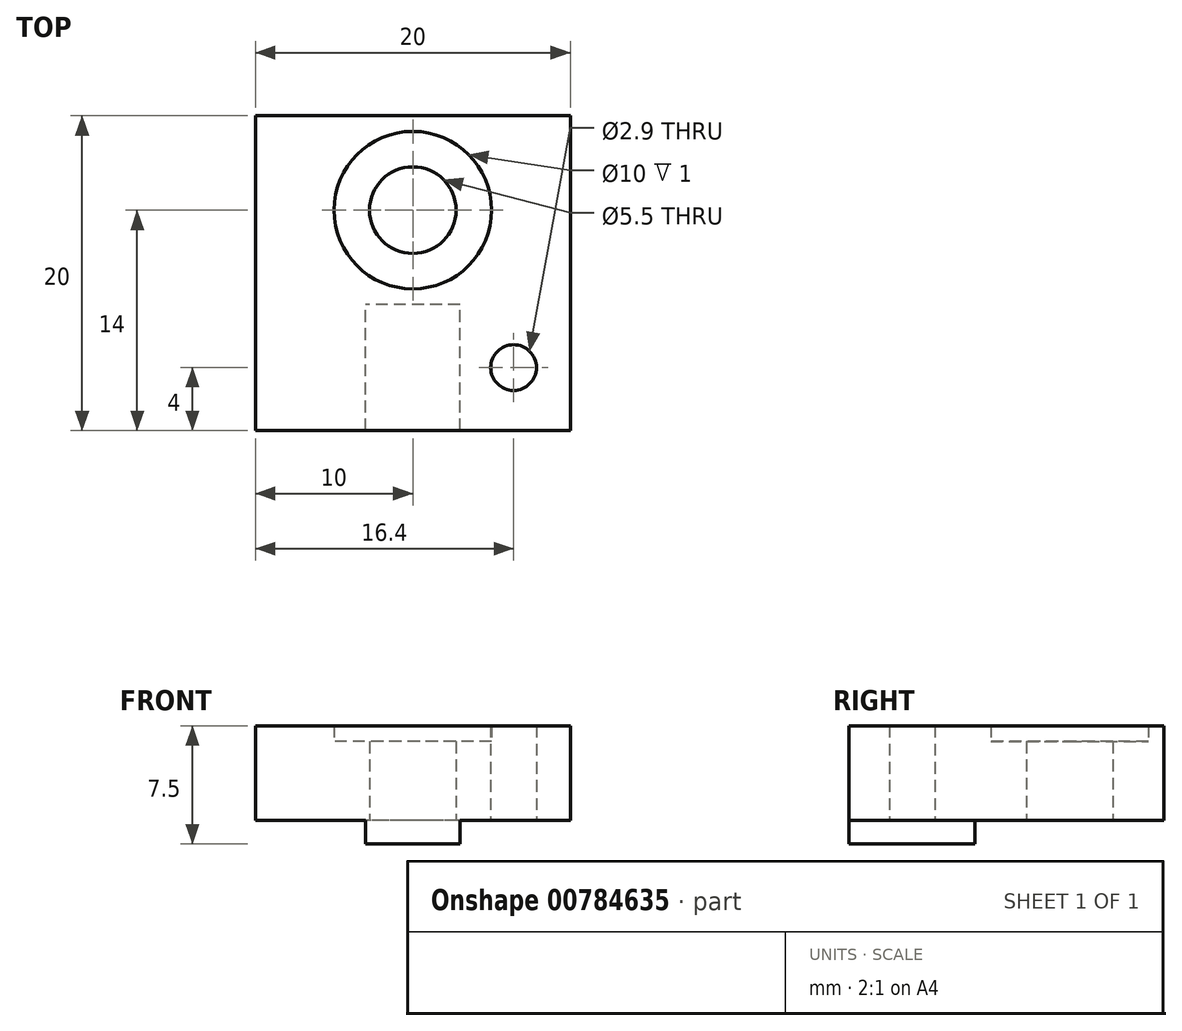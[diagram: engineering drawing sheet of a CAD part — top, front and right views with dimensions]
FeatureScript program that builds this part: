
annotation { "Feature Type Name" : "Feature", "Feature Type Description" : "" }
export const myFeature = defineFeature(function(context is Context, id is Id, definition is map)
    precondition{}
    {
        {
            var Q0;
            Q0=qCreatedBy(makeId("Top.planeOp"),FACE);
            var sketch = newSketch(context, id + "F0", { "sketchPlane" : qUnion([Q0])});
            skLineSegment(sketch, "E0.bottom", {"start": v(10, -10) * mm, "end": v(-10, -10) * mm});
            skLineSegment(sketch, "E0.top", {"start": v(10, 10) * mm, "end": v(-10, 10) * mm});
            skLineSegment(sketch, "E0.left", {"start": v(10, -10) * mm, "end": v(10, 10) * mm});
            skLineSegment(sketch, "E0.right", {"start": v(-10, -10) * mm, "end": v(-10, 10) * mm});
            skPoint(sketch, "E0.middle", {"position": v(0, 0) * mm});
            skCircle(sketch, "E1", {"center": v(0, 4) * mm, "radius": 2.75 * mm});
            skCircle(sketch, "E2", {"center": v(6.4, -6) * mm, "radius": 1.45 * mm});
            skLineSegment(sketch, "E3.bottom", {"start": v(3, -10) * mm, "end": v(-3, -10) * mm});
            skLineSegment(sketch, "E3.top", {"start": v(3, -2) * mm, "end": v(-3, -2) * mm});
            skLineSegment(sketch, "E3.left", {"start": v(3, -10) * mm, "end": v(3, -2) * mm});
            skLineSegment(sketch, "E3.right", {"start": v(-3, -10) * mm, "end": v(-3, -2) * mm});
            skPoint(sketch, "E3.middle", {"position": v(0, -6) * mm});
            skCircle(sketch, "E4", {"center": v(0, 4) * mm, "radius": 5 * mm});
            skSolve(sketch);
        }
        {
            var Q0;
            Q0=makeQuery(id+"F0.imprint","IMPRINT",FACE,{"disambiguationData":[TD([[makeQuery(id+"F0.imprint","IMPRINT",EDGE,{"derivedFrom":sQuery(id+"F0.wireOp",EDGE,"E0.bottom")}),-1.0]])]});
            var Q1;
            Q1=makeQuery(id+"F0.imprint","IMPRINT",FACE,{"disambiguationData":[TD([[makeQuery(id+"F0.imprint","IMPRINT",EDGE,{"derivedFrom":sQuery(id+"F0.wireOp",EDGE,"E3.top")}),1.0]])]});
            extrude(context, id + "F1", {"entities" : qUnion([Q0, Q1]), "depth" : 6 * mm, "offsetDistance" : 25 * mm});
        }
        {
            var Q0;
            Q0=makeQuery(id+"F0.imprint","IMPRINT",FACE,{"disambiguationData":[TD([[makeQuery(id+"F0.imprint","IMPRINT",EDGE,{"derivedFrom":sQuery(id+"F0.wireOp",EDGE,"E3.top")}),1.0]])]});
            extrude(context, id + "F2", {"entities" : qUnion([Q0]), "operationType" : NewBodyOperationType.ADD, "oppositeDirection" : true, "depth" : 1.5 * mm, "offsetDistance" : 25 * mm});
        }
        {
            var Q0;
            Q0=makeQuery(id+"F0.imprint","IMPRINT",FACE,{"disambiguationData":[TD([[makeQuery(id+"F0.imprint","IMPRINT",EDGE,{"derivedFrom":sQuery(id+"F0.wireOp",EDGE,"E1")}),-1.0]])]});
            extrude(context, id + "F3", {"entities" : qUnion([Q0]), "operationType" : NewBodyOperationType.ADD, "depth" : 5 * mm, "offsetDistance" : 25 * mm});
        }
    });
